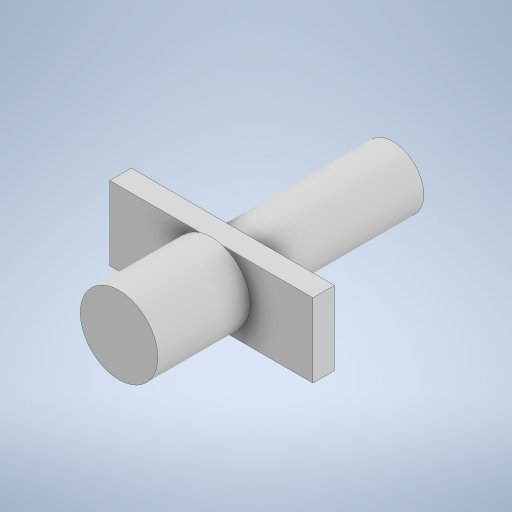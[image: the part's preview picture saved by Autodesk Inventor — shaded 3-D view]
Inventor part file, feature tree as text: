
AUTODESK INVENTOR PART (.ipt)
format: ipt  version: 2023 (Build 270158000, 158)  size: 254,464 bytes
history: native  units: in
note: dims shown in document units (in); Inventor stores cm internally (conversion verified against a paired STEP export)
features: extrude x3, sketch x3, projected_geometry x2
ambient origin geometry x8: Origin, YZ Plane, XZ Plane, XY Plane, X Axis, Y Axis, Z Axis, Center Point
bodies: Solid1 (feature_tree)
feature tree (8):
  extrude  "Extrusion1"  Depth=0.2362in
  extrude  "Extrusion2"  Depth=0.0689in
  extrude  "Extrusion3"  Depth=0.5118in
  sketch  "Sketch1"  dims[d0=0.6496in d1=0.2362in]
  sketch  "Sketch2"  dims[d2=0.0689in d3=0.0in d4=0.248in]
  projected_geometry  "Projected Loop1"
  sketch  "Sketch3"  dims[d5=0.2953in d6=0.0in d7=0.1969in d8=0.5118in d9=0.0in]
  projected_geometry  "Projected Loop2"
